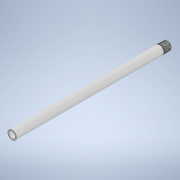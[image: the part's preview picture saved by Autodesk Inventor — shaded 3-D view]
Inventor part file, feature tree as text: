
AUTODESK INVENTOR PART (.ipt)
format: ipt  version: 2022 (Build 260153000, 153)  size: 805,376 bytes
history: native  units: in
note: dims shown in document units (in); Inventor stores cm internally (conversion verified against a paired STEP export)
features: extrude x1, sketch x1, revolve x1
ambient origin geometry x8: Origin, YZ Plane, XZ Plane, XY Plane, X Axis, Y Axis, Z Axis, Center Point
bodies: Solid1 (feature_tree)
feature tree (3):
  extrude  "Extrusion1"  [1 undecoded]
  sketch  "Sketch1"  dims[d0=15.0in d1=0.0in]
  revolve  "Revolve2"  [1 undecoded]
note: 2 required parameter values undecoded (feature->parameter linkage not recoverable at this tier; creation-order binding heuristic only, values carry confidence <= 0.55)
